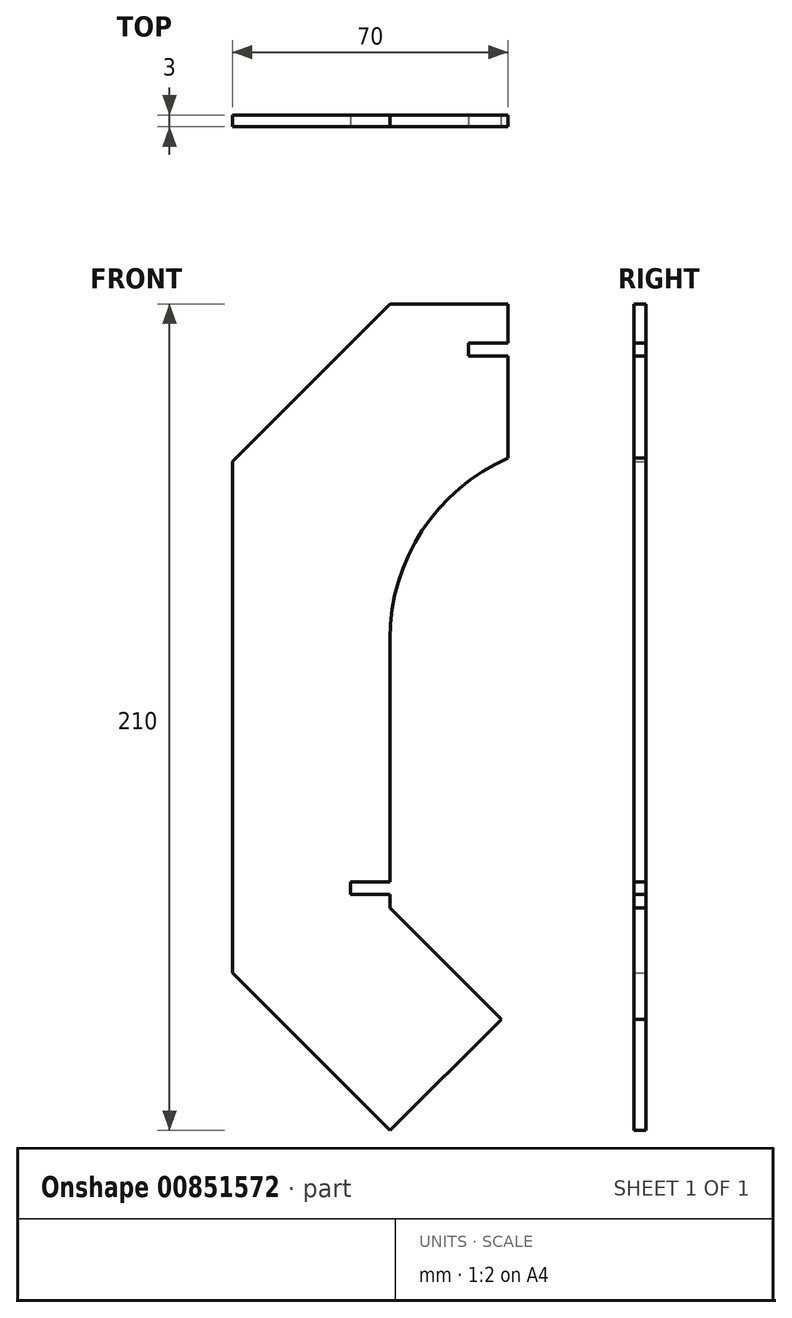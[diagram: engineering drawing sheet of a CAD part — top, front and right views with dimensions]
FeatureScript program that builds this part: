
annotation { "Feature Type Name" : "Feature", "Feature Type Description" : "" }
export const myFeature = defineFeature(function(context is Context, id is Id, definition is map)
    precondition{}
    {
        {
            var Q0;
            Q0=qCreatedBy(makeId("Front.planeOp"),FACE);
            var sketch = newSketch(context, id + "F0", { "sketchPlane" : qUnion([Q0])});
            skLineSegment(sketch, "E0", {"start": v(0, 0) * mm, "end": v(-50, 0) * mm});
            skLineSegment(sketch, "E1", {"start": v(-50, 0) * mm, "end": v(-90, -40) * mm});
            skLineSegment(sketch, "E2", {"start": v(-90, -40) * mm, "end": v(-90, -170) * mm});
            skLineSegment(sketch, "E3", {"start": v(-90, -170) * mm, "end": v(-50, -210) * mm});
            skLineSegment(sketch, "E4", {"start": v(-50, -210) * mm, "end": v(-21.72, -181.72) * mm});
            skLineSegment(sketch, "E5", {"start": v(-21.72, -181.72) * mm, "end": v(-50, -153.43) * mm});
            skArc(sketch, "E6", {"start": v(0, -35) * mm, "mid": v(-35.36, -49.64) * mm, "end": v(-50, -85) * mm});
            skLineSegment(sketch, "E7", {"start": v(-50, -85) * mm, "end": v(-50, -153.43) * mm});
            skLineSegment(sketch, "E8", {"start": v(0, 0) * mm, "end": v(0, -35) * mm});
            skSolve(sketch);
        }
        {
            var Q0;
            Q0=makeQuery(id+"F0.imprint","IMPRINT",FACE,{"disambiguationData":[TD([[makeQuery(id+"F0.imprint","IMPRINT",EDGE,{"derivedFrom":sQuery(id+"F0.wireOp",EDGE,"E0")}),1.0]])]});
            extrude(context, id + "F1", {"entities" : qUnion([Q0]), "endBound" : BoundingType.SYMMETRIC, "depth" : 3 * mm, "offsetDistance" : 25 * mm});
        }
        {
            var Q0;
            Q0=makeQuery(id+"F1.opExtrude","CAP_FACE",FACE,{"disambiguationData":[OSD([sQuery(id+"F0.wireOp",EDGE,"E0"),sQuery(id+"F0.wireOp",EDGE,"E1"),sQuery(id+"F0.wireOp",EDGE,"E2"),sQuery(id+"F0.wireOp",EDGE,"E3"),sQuery(id+"F0.wireOp",EDGE,"E4"),sQuery(id+"F0.wireOp",EDGE,"E5"),sQuery(id+"F0.wireOp",EDGE,"E6"),sQuery(id+"F0.wireOp",EDGE,"E7"),sQuery(id+"F0.wireOp",EDGE,"E8")])],"isStart":false});
            var sketch = newSketch(context, id + "F2", { "sketchPlane" : qUnion([Q0])});
            skLineSegment(sketch, "E9", {"start": v(-20, 0) * mm, "end": v(-20, -10) * mm});
            skLineSegment(sketch, "E10", {"start": v(-20, -10) * mm, "end": v(-30, -10) * mm});
            skLineSegment(sketch, "E11", {"start": v(-30, -10) * mm, "end": v(-30, -13.2) * mm});
            skLineSegment(sketch, "E12", {"start": v(-30, -13.2) * mm, "end": v(-20, -13.2) * mm});
            skLineSegment(sketch, "E13", {"start": v(-20, -13.2) * mm, "end": v(-20, -39.17) * mm});
            skArc(sketch, "E14.0", {"start": v(0, -35) * mm, "mid": v(-10.22, -36.05) * mm, "end": v(-20, -39.17) * mm});
            skPoint(sketch, "E15.orphan", {"position": v(-50, -85) * mm});
            skLineSegment(sketch, "E16", {"start": v(-20, 0) * mm, "end": v(0, 0) * mm});
            skLineSegment(sketch, "E17", {"start": v(0, 0) * mm, "end": v(0, -35) * mm});
            skLineSegment(sketch, "E18", {"start": v(0, 0) * mm, "end": v(0, 26.78) * mm, "construction": true});
            skLineSegment(sketch, "E19.bottom", {"start": v(-60, -146.8) * mm, "end": v(-50, -146.8) * mm});
            skLineSegment(sketch, "E19.top", {"start": v(-60, -150) * mm, "end": v(-50, -150) * mm});
            skLineSegment(sketch, "E19.left", {"start": v(-60, -146.8) * mm, "end": v(-60, -150) * mm});
            skLineSegment(sketch, "E19.right", {"start": v(-50, -146.8) * mm, "end": v(-50, -150) * mm});
            skSolve(sketch);
        }
        {
            var Q0;
            Q0=qSketchRegion(id+"F2",true);
            extrude(context, id + "F3", {"entities" : qUnion([Q0]), "operationType" : NewBodyOperationType.REMOVE, "endBound" : BoundingType.THROUGH_ALL, "oppositeDirection" : true, "depth" : 25 * mm});
        }
    });
